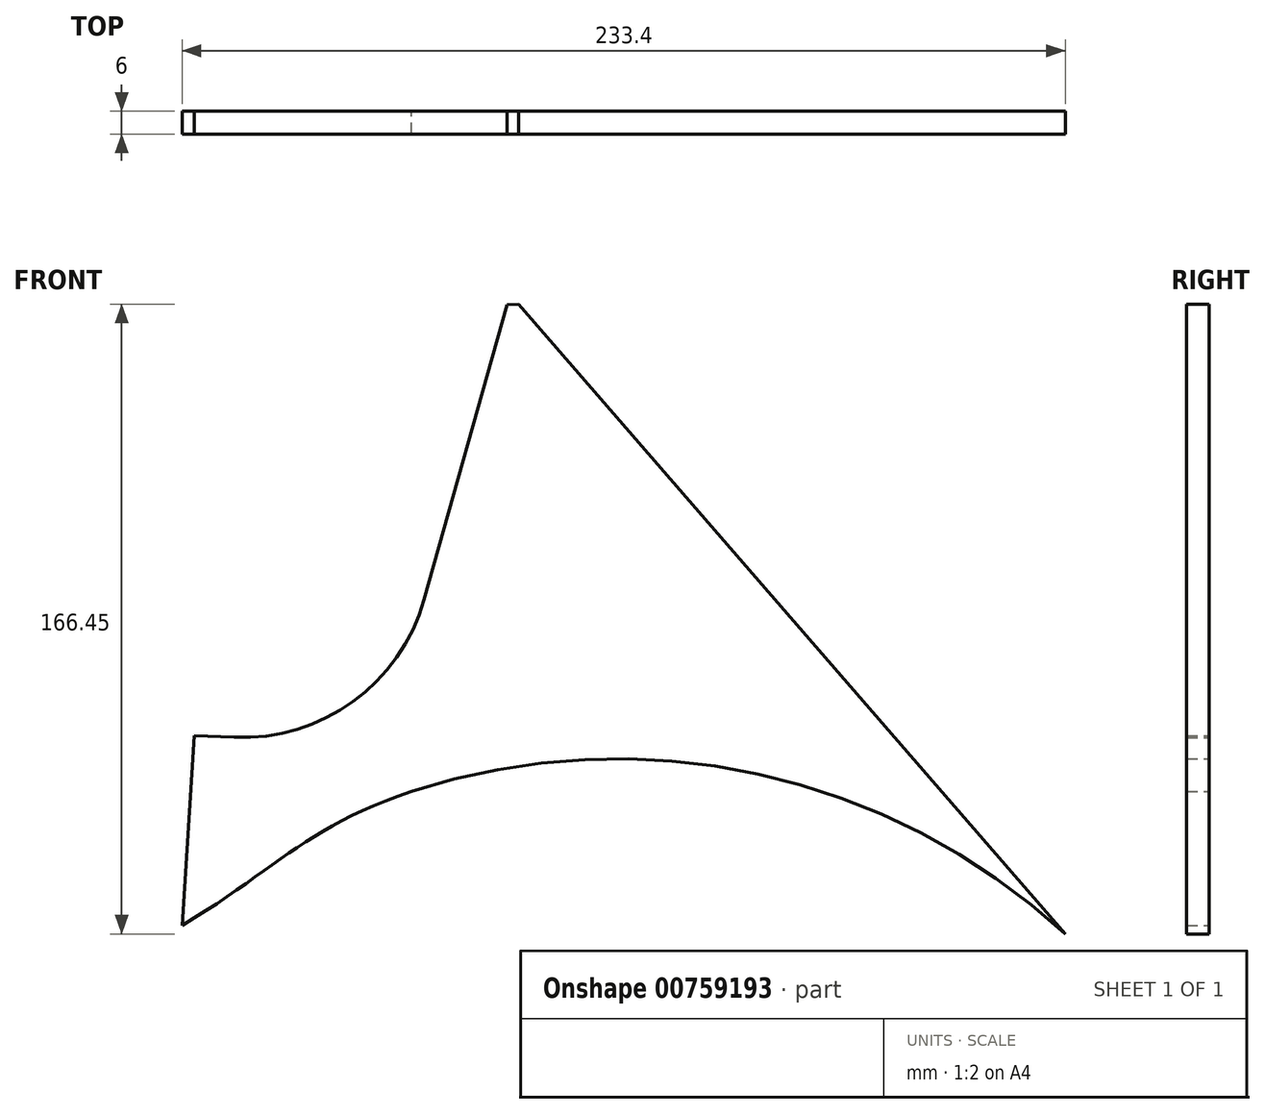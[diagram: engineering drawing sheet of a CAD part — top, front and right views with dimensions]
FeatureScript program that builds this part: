
annotation { "Feature Type Name" : "Feature", "Feature Type Description" : "" }
export const myFeature = defineFeature(function(context is Context, id is Id, definition is map)
    precondition{}
    {
        {
            var Q0;
            Q0=qCreatedBy(makeId("Front.planeOp"),FACE);
            var sketch = newSketch(context, id + "F0", { "sketchPlane" : qUnion([Q0])});
            skPoint(sketch, "E0.visualSharp", {"position": v(-52.42, 176.48) * mm});
            skPoint(sketch, "E1.visualSharp", {"position": v(-61.23, 192.89) * mm});
            skLineSegment(sketch, "E2", {"start": v(-116.98, 146.43) * mm, "end": v(-113.78, 196.57) * mm});
            skLineSegment(sketch, "E3", {"start": v(-28.1, 310.61) * mm, "end": v(116.42, 144.16) * mm});
            skLineSegment(sketch, "E4", {"start": v(-31.1, 310.52) * mm, "end": v(-28.1, 310.61) * mm});
            skLineSegment(sketch, "E5.trimOffspring", {"start": v(-113.78, 196.57) * mm, "end": v(-103.3, 196.12) * mm});
            skLineSegment(sketch, "E6", {"start": v(-53.06, 232.53) * mm, "end": v(-31.1, 310.52) * mm});
            skPoint(sketch, "E7.visualSharp", {"position": v(-63.78, 194.46) * mm});
            skArc(sketch, "E7.filletArc", {"start": v(-103.3, 196.12) * mm, "mid": v(-71.85, 205.6) * mm, "end": v(-53.06, 232.53) * mm});
            skPoint(sketch, "E8.visualSharp", {"position": v(-119.91, 271.82) * mm});
            skFitSpline(sketch, "E9", {"points": [v(-295.34, 82.4) * mm, v(-116.98, 146.43) * mm, v(-56.41, 181.8) * mm], "startDerivative": vector(217.3, 5.56) * mm, "endDerivative": vector(222.4, 75.34) * mm});
            skArc(sketch, "E10.trimOffspring", {"start": v(116.42, 144.16) * mm, "mid": v(35.1, 186.43) * mm, "end": v(-56.41, 181.8) * mm});
            skSolve(sketch);
        }
        {
            var Q0;
            Q0=qSketchRegion(id+"F0",true);
            extrude(context, id + "F1", {"entities" : qUnion([Q0]), "depth" : 6 * mm, "offsetDistance" : 25 * mm});
        }
    });
